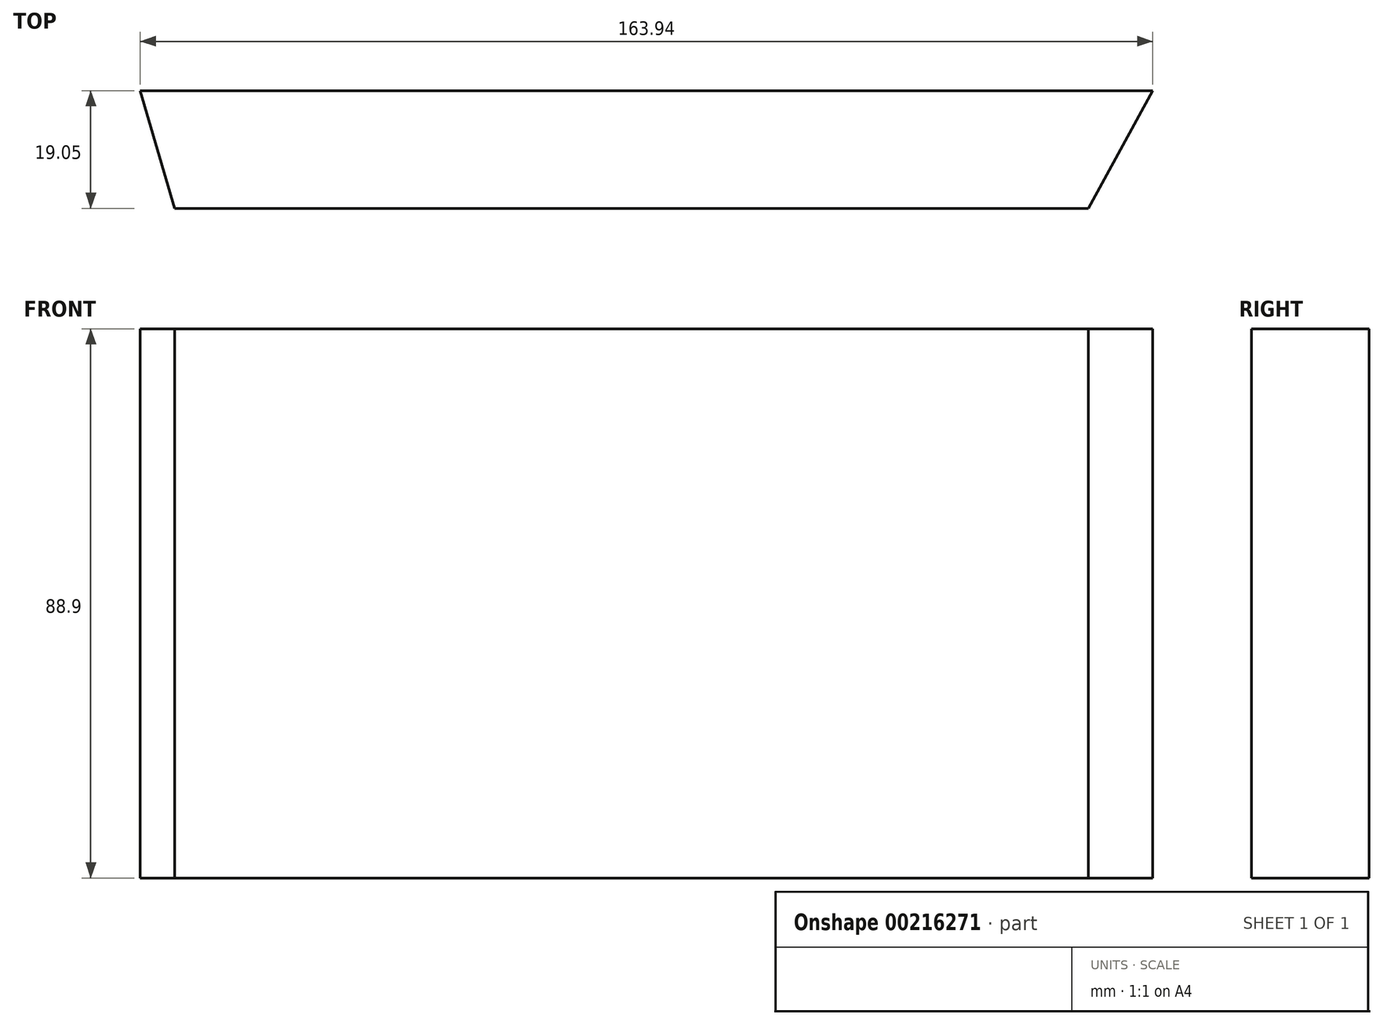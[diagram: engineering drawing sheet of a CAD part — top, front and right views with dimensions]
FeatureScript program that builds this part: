
annotation { "Feature Type Name" : "Feature", "Feature Type Description" : "" }
export const myFeature = defineFeature(function(context is Context, id is Id, definition is map)
    precondition{}
    {
        {
            var Q0;
            Q0=qCreatedBy(makeId("Front.planeOp"),FACE);
            var sketch = newSketch(context, id + "F0", { "sketchPlane" : qUnion([Q0])});
            skLineSegment(sketch, "E0", {"start": v(-1215.24, -1113.1) * mm, "end": v(-1051.3, -1113.1) * mm});
            skLineSegment(sketch, "E1", {"start": v(-1051.3, -1113.1) * mm, "end": v(-1051.3, -1024.2) * mm});
            skLineSegment(sketch, "E2", {"start": v(-1051.3, -1024.2) * mm, "end": v(-1215.24, -1024.2) * mm});
            skLineSegment(sketch, "E3", {"start": v(-1215.24, -1024.2) * mm, "end": v(-1215.24, -1113.1) * mm});
            skSolve(sketch);
        }
        {
            var Q0;
            Q0=makeQuery(id+"F0.imprint","IMPRINT",FACE,{"disambiguationData":[TD([[makeQuery(id+"F0.imprint","IMPRINT",EDGE,{"derivedFrom":sQuery(id+"F0.wireOp",EDGE,"E0")}),1.0]])]});
            extrude(context, id + "F1", {"entities" : qUnion([Q0]), "depth" : 19.05 * mm});
        }
        {
            var Q0;
            Q0=makeQuery(id+"F1.opExtrude","SWEPT_FACE",FACE,{"disambiguationData":[OSD([sQuery(id+"F0.wireOp",EDGE,"E2")])]});
            var sketch = newSketch(context, id + "F2", { "sketchPlane" : qUnion([Q0])});
            skLineSegment(sketch, "E4", {"start": v(-1215.24, 0) * mm, "end": v(-1209.68, -19.05) * mm});
            skLineSegment(sketch, "E5", {"start": v(-1209.68, -19.05) * mm, "end": v(-1215.24, -19.05) * mm});
            skLineSegment(sketch, "E6", {"start": v(-1215.24, -19.05) * mm, "end": v(-1215.24, 0) * mm});
            skLineSegment(sketch, "E7", {"start": v(-1051.3, 0) * mm, "end": v(-1051.3, -19.05) * mm});
            skLineSegment(sketch, "E8", {"start": v(-1051.3, -19.05) * mm, "end": v(-1061.74, -19.05) * mm});
            skLineSegment(sketch, "E9", {"start": v(-1061.74, -19.05) * mm, "end": v(-1051.3, 0) * mm});
            skSolve(sketch);
        }
        {
            var Q0;
            Q0=makeQuery(id+"F2.imprint","IMPRINT",FACE,{"disambiguationData":[TD([[makeQuery(id+"F2.imprint","IMPRINT",EDGE,{"derivedFrom":sQuery(id+"F2.wireOp",EDGE,"E4")}),-1.0]])]});
            extrude(context, id + "F3", {"entities" : qUnion([Q0]), "operationType" : NewBodyOperationType.REMOVE, "endBound" : BoundingType.THROUGH_ALL, "oppositeDirection" : true, "depth" : 25.4 * mm});
        }
        {
            var Q0;
            Q0=makeQuery(id+"F2.imprint","IMPRINT",FACE,{"disambiguationData":[TD([[makeQuery(id+"F2.imprint","IMPRINT",EDGE,{"derivedFrom":sQuery(id+"F2.wireOp",EDGE,"E7")}),1.0]])]});
            extrude(context, id + "F4", {"entities" : qUnion([Q0]), "operationType" : NewBodyOperationType.REMOVE, "endBound" : BoundingType.THROUGH_ALL, "oppositeDirection" : true, "depth" : 25.4 * mm});
        }
    });
